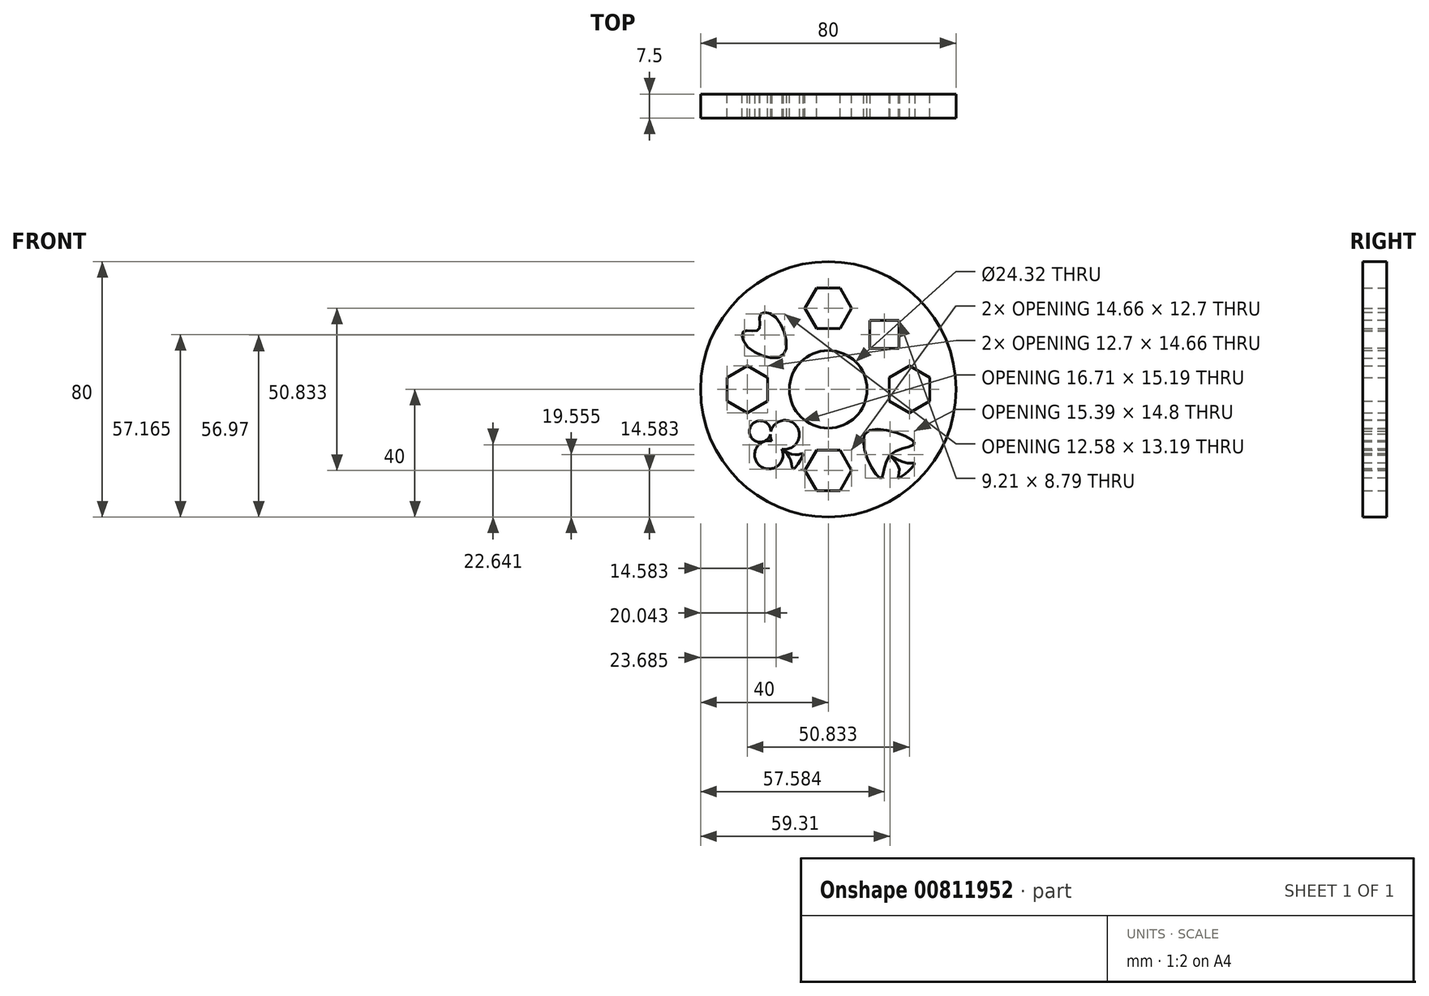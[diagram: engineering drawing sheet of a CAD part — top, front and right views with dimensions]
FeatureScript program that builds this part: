
annotation { "Feature Type Name" : "Feature", "Feature Type Description" : "" }
export const myFeature = defineFeature(function(context is Context, id is Id, definition is map)
    precondition{}
    {
        {
            var Q0;
            Q0=qCreatedBy(makeId("Front.planeOp"),FACE);
            var sketch = newSketch(context, id + "F0", { "sketchPlane" : qUnion([Q0])});
            skCircle(sketch, "E0", {"center": v(0, 0) * mm, "radius": 40 * mm});
            skCircle(sketch, "E1", {"center": v(0, 0) * mm, "radius": 12.16 * mm});
            skCircle(sketch, "E2.cCircle", {"center": v(0, 25.42) * mm, "radius": 6.35 * mm, "construction": true});
            skLineSegment(sketch, "E2.0", {"start": v(3.67, 19.07) * mm, "end": v(-3.67, 19.07) * mm});
            skLineSegment(sketch, "E2.1", {"start": v(-3.67, 19.07) * mm, "end": v(-7.33, 25.42) * mm});
            skLineSegment(sketch, "E2.2", {"start": v(-7.33, 25.42) * mm, "end": v(-3.67, 31.77) * mm});
            skLineSegment(sketch, "E2.3", {"start": v(-3.67, 31.77) * mm, "end": v(3.67, 31.77) * mm});
            skLineSegment(sketch, "E2.4", {"start": v(3.67, 31.77) * mm, "end": v(7.33, 25.42) * mm});
            skLineSegment(sketch, "E2.5", {"start": v(7.33, 25.42) * mm, "end": v(3.67, 19.07) * mm});
            skPoint(sketch, "E2.0.midPoint", {"position": v(0, 19.07) * mm});
            skLineSegment(sketch, "E3.1.0", {"start": v(-31.77, 3.67) * mm, "end": v(-25.42, 7.33) * mm});
            skLineSegment(sketch, "E3.1.1", {"start": v(-31.77, -3.67) * mm, "end": v(-31.77, 3.67) * mm});
            skLineSegment(sketch, "E3.1.2", {"start": v(-25.42, -7.33) * mm, "end": v(-31.77, -3.67) * mm});
            skCircle(sketch, "E3.1.3", {"center": v(-25.42, 0) * mm, "radius": 6.35 * mm, "construction": true});
            skLineSegment(sketch, "E3.1.4", {"start": v(-25.42, 7.33) * mm, "end": v(-19.07, 3.67) * mm});
            skLineSegment(sketch, "E3.1.5", {"start": v(-19.07, -3.67) * mm, "end": v(-25.42, -7.33) * mm});
            skLineSegment(sketch, "E3.1.6", {"start": v(-19.07, 3.67) * mm, "end": v(-19.07, -3.67) * mm});
            skPoint(sketch, "E3.1.7", {"position": v(-19.07, 0) * mm});
            skLineSegment(sketch, "E3.2.0", {"start": v(-3.67, -31.77) * mm, "end": v(-7.33, -25.42) * mm});
            skLineSegment(sketch, "E3.2.1", {"start": v(3.67, -31.77) * mm, "end": v(-3.67, -31.77) * mm});
            skLineSegment(sketch, "E3.2.2", {"start": v(7.33, -25.42) * mm, "end": v(3.67, -31.77) * mm});
            skCircle(sketch, "E3.2.3", {"center": v(0, -25.42) * mm, "radius": 6.35 * mm, "construction": true});
            skLineSegment(sketch, "E3.2.4", {"start": v(-7.33, -25.42) * mm, "end": v(-3.67, -19.07) * mm});
            skLineSegment(sketch, "E3.2.5", {"start": v(3.67, -19.07) * mm, "end": v(7.33, -25.42) * mm});
            skLineSegment(sketch, "E3.2.6", {"start": v(-3.67, -19.07) * mm, "end": v(3.67, -19.07) * mm});
            skPoint(sketch, "E3.2.7", {"position": v(0, -19.07) * mm});
            skLineSegment(sketch, "E3.3.0", {"start": v(31.77, -3.67) * mm, "end": v(25.42, -7.33) * mm});
            skLineSegment(sketch, "E3.3.1", {"start": v(31.77, 3.67) * mm, "end": v(31.77, -3.67) * mm});
            skLineSegment(sketch, "E3.3.2", {"start": v(25.42, 7.33) * mm, "end": v(31.77, 3.67) * mm});
            skCircle(sketch, "E3.3.3", {"center": v(25.42, 0) * mm, "radius": 6.35 * mm, "construction": true});
            skLineSegment(sketch, "E3.3.4", {"start": v(25.42, -7.33) * mm, "end": v(19.07, -3.67) * mm});
            skLineSegment(sketch, "E3.3.5", {"start": v(19.07, 3.67) * mm, "end": v(25.42, 7.33) * mm});
            skLineSegment(sketch, "E3.3.6", {"start": v(19.07, -3.67) * mm, "end": v(19.07, 3.67) * mm});
            skPoint(sketch, "E3.3.7", {"position": v(19.07, 0) * mm});
            skText(sketch, "E4", { "text": "AP", "fontName": "OpenSans-Regular.ttf"});
            const initialGuessF0  = {"E4": [-0.1348, -0.05731, 1, 0, 0.01235]};
            skSetInitialGuess(sketch, initialGuessF0);
            skSolve(sketch);
        }
        {
            var Q0;
            Q0=makeQuery(id+"F0.imprint","IMPRINT",FACE,{"disambiguationData":[TD([[makeQuery(id+"F0.imprint","IMPRINT",EDGE,{"derivedFrom":sQuery(id+"F0.wireOp",EDGE,"E0")}),1.0]])]});
            extrude(context, id + "F1", {"entities" : qUnion([Q0]), "depth" : 7.5 * mm, "offsetDistance" : 25 * mm, "symmetric" : true});
        }
        {
            var Q0;
            Q0=qCreatedBy(makeId("Front.planeOp"),FACE);
            var sketch = newSketch(context, id + "F2", { "sketchPlane" : qUnion([Q0])});
            skFitSpline(sketch, "E5", {"points": [v(-14.03, 10.89) * mm, v(-25.12, 13.19) * mm, v(-26.38, 18.21) * mm, v(-21.77, 18.63) * mm, v(-21.35, 23.24) * mm, v(-16.75, 22.82) * mm, v(-14.03, 10.89) * mm]});
            skFitSpline(sketch, "E6", {"points": [v(19.26, -20.73) * mm, v(16.33, -27.84) * mm, v(11.72, -13.6) * mm, v(27, -16.75) * mm, v(19.26, -20.73) * mm]});
            skFitSpline(sketch, "E7", {"points": [v(19.26, -20.73) * mm, v(22.19, -24.91) * mm, v(21.98, -27.84) * mm, v(27, -23.45) * mm, v(24.5, -23.03) * mm, v(19.26, -20.73) * mm]});
            skLineSegment(sketch, "E8.bottom", {"start": v(12.98, 12.77) * mm, "end": v(22.19, 12.77) * mm});
            skLineSegment(sketch, "E8.top", {"start": v(12.98, 21.56) * mm, "end": v(22.19, 21.56) * mm});
            skLineSegment(sketch, "E8.left", {"start": v(12.98, 12.77) * mm, "end": v(12.98, 21.56) * mm});
            skLineSegment(sketch, "E8.right", {"start": v(22.19, 12.77) * mm, "end": v(22.19, 21.56) * mm});
            skCircle(sketch, "E9", {"center": v(-21.35, -13.19) * mm, "radius": 3.35 * mm});
            skCircle(sketch, "E10", {"center": v(-18.63, -20.52) * mm, "radius": 4.44 * mm});
            skCircle(sketch, "E11", {"center": v(-13.6, -14.24) * mm, "radius": 4.53 * mm});
            skFitSpline(sketch, "E12", {"points": [v(-14.6, -18.65) * mm, v(-11.93, -21.77) * mm, v(-10.89, -24.91) * mm, v(-7.96, -20.3) * mm, v(-10.26, -20.52) * mm, v(-14.6, -18.65) * mm]});
            skSolve(sketch);
        }
        {
            var Q0;
            Q0 = qSketchRegion(id + "F2", true);
            extrude(context, id + "F3", {"entities" : qUnion([Q0]), "operationType" : NewBodyOperationType.REMOVE, "oppositeDirection" : true, "depth" : 25 * mm, "offsetDistance" : 25 * mm, "symmetric" : true});
        }
    });
